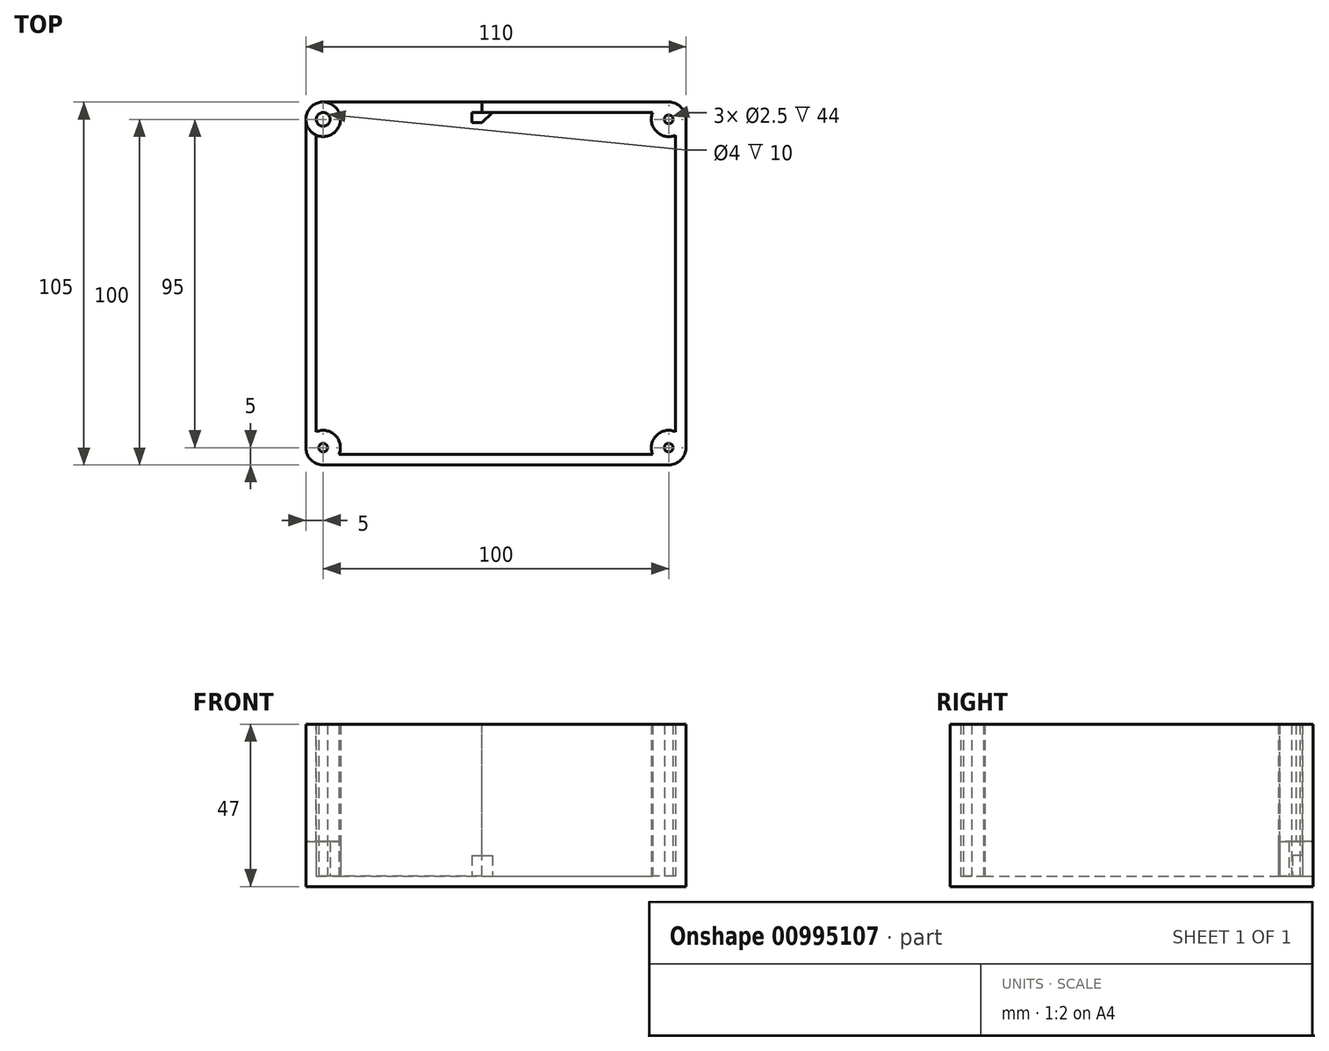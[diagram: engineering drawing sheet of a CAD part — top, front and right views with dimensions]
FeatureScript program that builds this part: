
annotation { "Feature Type Name" : "Feature", "Feature Type Description" : "" }
export const myFeature = defineFeature(function(context is Context, id is Id, definition is map)
    precondition{}
    {
        {
            var Q0;
            Q0=qCreatedBy(makeId("Top.planeOp"),FACE);
            var sketch = newSketch(context, id + "F0", { "sketchPlane" : qUnion([Q0])});
            skLineSegment(sketch, "E0.bottom", {"start": v(-55, -52.5) * mm, "end": v(55, -52.5) * mm});
            skLineSegment(sketch, "E0.top", {"start": v(-55, 52.5) * mm, "end": v(55, 52.5) * mm});
            skLineSegment(sketch, "E0.left", {"start": v(-55, -52.5) * mm, "end": v(-55, 52.5) * mm});
            skLineSegment(sketch, "E0.right", {"start": v(55, -52.5) * mm, "end": v(55, 52.5) * mm});
            skPoint(sketch, "E0.middle", {"position": v(0, 0) * mm});
            skSolve(sketch);
        }
        {
            var Q0;
            Q0 = qSketchRegion(id + "F0", true);
            extrude(context, id + "F1", {"entities" : qUnion([Q0]), "endBound" : BoundingType.SYMMETRIC, "depth" : 47 * mm, "offsetDistance" : 25 * mm});
        }
        {
            var Q0;
            Q0=makeQuery(id+"F1.opExtrude","SWEPT_EDGE",EDGE,{"disambiguationData":[OSD([sQuery(id+"F0.wireOp",EDGE,"E0.bottom"),sQuery(id+"F0.wireOp",EDGE,"E0.right")])]});
            var Q1;
            Q1=makeQuery(id+"F1.opExtrude","SWEPT_EDGE",EDGE,{"disambiguationData":[OSD([sQuery(id+"F0.wireOp",EDGE,"E0.bottom"),sQuery(id+"F0.wireOp",EDGE,"E0.left")])]});
            var Q2;
            Q2=makeQuery(id+"F1.opExtrude","SWEPT_EDGE",EDGE,{"disambiguationData":[OSD([sQuery(id+"F0.wireOp",EDGE,"E0.top"),sQuery(id+"F0.wireOp",EDGE,"E0.left")])]});
            var Q3;
            Q3=makeQuery(id+"F1.opExtrude","SWEPT_EDGE",EDGE,{"disambiguationData":[OSD([sQuery(id+"F0.wireOp",EDGE,"E0.top"),sQuery(id+"F0.wireOp",EDGE,"E0.right")])]});
            fillet(context, id + "F2", {"entities" : qUnion([Q0, Q1, Q2, Q3]), "radius" : 5 * mm, "tangentPropagation" : true, "allowEdgeOverflow" : false});
        }
        {
            var Q0;
            Q0=makeQuery(id+"F1.opExtrude","CAP_FACE",FACE,{"disambiguationData":[OSD([sQuery(id+"F0.wireOp",EDGE,"E0.bottom"),sQuery(id+"F0.wireOp",EDGE,"E0.top"),sQuery(id+"F0.wireOp",EDGE,"E0.left"),sQuery(id+"F0.wireOp",EDGE,"E0.right")])],"isStart":false});
            shell(context, id + "F3", {"entities" : qUnion([Q0]), "thickness" : 3 * mm});
        }
        {
            var Q0;
            Q0=makeQuery(id+"F3.opShell","OFFSET_FACE",FACE,{"disambiguationData":[OSD([sQuery(id+"F0.wireOp",EDGE,"E0.bottom"),sQuery(id+"F0.wireOp",EDGE,"E0.top"),sQuery(id+"F0.wireOp",EDGE,"E0.left"),sQuery(id+"F0.wireOp",EDGE,"E0.right")])]});
            var sketch = newSketch(context, id + "F4", { "sketchPlane" : qUnion([Q0])});
            skCircle(sketch, "E1", {"center": v(-50, -47.5) * mm, "radius": 5 * mm});
            skCircle(sketch, "E2", {"center": v(50, -47.5) * mm, "radius": 5 * mm});
            skCircle(sketch, "E3", {"center": v(50, 47.5) * mm, "radius": 5 * mm});
            skSolve(sketch);
        }
        {
            var Q0;
            Q0 = qSketchRegion(id + "F4", true);
            var Q1;
            Q1=makeQuery(id+"F1.opExtrude","CAP_FACE",FACE,{"disambiguationData":[OSD([sQuery(id+"F0.wireOp",EDGE,"E0.bottom"),sQuery(id+"F0.wireOp",EDGE,"E0.top"),sQuery(id+"F0.wireOp",EDGE,"E0.left"),sQuery(id+"F0.wireOp",EDGE,"E0.right")])],"isStart":false});
            extrude(context, id + "F5", {"entities" : qUnion([Q0]), "operationType" : NewBodyOperationType.ADD, "endBound" : BoundingType.UP_TO_SURFACE, "depth" : 25 * mm, "endBoundEntityFace" : qUnion([Q1]), "offsetDistance" : 25 * mm});
        }
        {
            var Q0;
            Q0=makeQuery(id+"F3.opShell","OFFSET_FACE",FACE,{"disambiguationData":[OSD([sQuery(id+"F0.wireOp",EDGE,"E0.bottom"),sQuery(id+"F0.wireOp",EDGE,"E0.top"),sQuery(id+"F0.wireOp",EDGE,"E0.left"),sQuery(id+"F0.wireOp",EDGE,"E0.right")])]});
            var sketch = newSketch(context, id + "F6", { "sketchPlane" : qUnion([Q0])});
            skCircle(sketch, "E4", {"center": v(-50, -47.5) * mm, "radius": 1.25 * mm});
            skCircle(sketch, "E5", {"center": v(50, -47.5) * mm, "radius": 1.25 * mm});
            skCircle(sketch, "E6", {"center": v(50, 47.5) * mm, "radius": 1.25 * mm});
            skSolve(sketch);
        }
        {
            var Q0;
            Q0 = qSketchRegion(id + "F6", true);
            var Q1;
            Q1=makeQuery(id+"F5.boolean.opBoolean","MERGE",FACE,{"derivedFrom":[makeQuery(id+"F1.opExtrude","CAP_FACE",FACE,{"disambiguationData":[OSD([sQuery(id+"F0.wireOp",EDGE,"E0.bottom"),sQuery(id+"F0.wireOp",EDGE,"E0.top"),sQuery(id+"F0.wireOp",EDGE,"E0.left"),sQuery(id+"F0.wireOp",EDGE,"E0.right")])],"isStart":false}),makeQuery(id+"F5.opExtrude","CAP_FACE",FACE,{"disambiguationData":[OSD([sQuery(id+"F4.wireOp",EDGE,"E1")])],"isStart":false}),makeQuery(id+"F5.opExtrude","CAP_FACE",FACE,{"disambiguationData":[OSD([sQuery(id+"F4.wireOp",EDGE,"E2")])],"isStart":false}),makeQuery(id+"F5.opExtrude","CAP_FACE",FACE,{"disambiguationData":[OSD([sQuery(id+"F4.wireOp",EDGE,"E3")])],"isStart":false}),makeQuery(id+"F5.opExtrude","CAP_FACE",FACE,{"disambiguationData":[OSD([sQuery(id+"F4.wireOp",EDGE,"hSmFbgNi-J2mV-61Hc-GoRM-wuo9VpQavHXK")])],"isStart":false})]});
            extrude(context, id + "F7", {"entities" : qUnion([Q0]), "operationType" : NewBodyOperationType.REMOVE, "endBound" : BoundingType.UP_TO_SURFACE, "depth" : 25 * mm, "endBoundEntityFace" : qUnion([Q1]), "offsetDistance" : 25 * mm});
        }
        {
            var Q0;
            Q0=makeQuery(id+"FNmOlcrzUNOjlDW_1.boolean.opBoolean","MERGE",FACE,{"derivedFrom":[makeQuery(id+"F1.opExtrude","CAP_FACE",FACE,{"disambiguationData":[OSD([sQuery(id+"F0.wireOp",EDGE,"E0.bottom"),sQuery(id+"F0.wireOp",EDGE,"E0.top"),sQuery(id+"F0.wireOp",EDGE,"E0.left"),sQuery(id+"F0.wireOp",EDGE,"E0.right")])],"isStart":false}),makeQuery(id+"FNmOlcrzUNOjlDW_1.opExtrude","CAP_FACE",FACE,{"disambiguationData":[OSD([sQuery(id+"Fl73VWrxdAUel7K_1.wireOp",EDGE,"jCLqAK4i-84Nv-s7N0-ioBH-w4pOyGSMhPc0.bottom"),sQuery(id+"Fl73VWrxdAUel7K_1.wireOp",EDGE,"jCLqAK4i-84Nv-s7N0-ioBH-w4pOyGSMhPc0.top"),sQuery(id+"Fl73VWrxdAUel7K_1.wireOp",EDGE,"jCLqAK4i-84Nv-s7N0-ioBH-w4pOyGSMhPc0.left"),sQuery(id+"Fl73VWrxdAUel7K_1.wireOp",EDGE,"jCLqAK4i-84Nv-s7N0-ioBH-w4pOyGSMhPc0.right"),sQuery(id+"Fl73VWrxdAUel7K_1.wireOp",EDGE,"joEXNwAF-BjP9-4Sa6-PMDD-CcShLHSFX7Nu"),sQuery(id+"Fl73VWrxdAUel7K_1.wireOp",EDGE,"PspjCuC4-ct6j-beC7-JPcA-AMhMl90AcsFd"),sQuery(id+"Fl73VWrxdAUel7K_1.wireOp",EDGE,"BXyMQO9f-R41G-yzOT-ZLec-crP29x3uA3BI"),sQuery(id+"Fl73VWrxdAUel7K_1.wireOp",EDGE,"BY3yu8Kp-6BFw-ywOW-VnpQ-I8gklTRwLebo")])],"isStart":true})]});
            var sketch = newSketch(context, id + "F8", { "sketchPlane" : qUnion([Q0])});
            skLineSegment(sketch, "E7.bottom", {"start": v(-52, 52.5) * mm, "end": v(-4, 52.5) * mm});
            skLineSegment(sketch, "E7.top", {"start": v(-52, 47.5) * mm, "end": v(-4, 47.5) * mm});
            skLineSegment(sketch, "E7.left", {"start": v(-52, 52.5) * mm, "end": v(-52, 47.5) * mm});
            skLineSegment(sketch, "E7.right", {"start": v(-4, 52.5) * mm, "end": v(-4, 47.5) * mm});
            skSolve(sketch);
        }
        {
            var Q0;
            Q0 = qSketchRegion(id + "F8", true);
            var Q1;
            Q1=makeQuery(id+"F3.opShell","OFFSET_FACE",FACE,{"disambiguationData":[OSD([sQuery(id+"F0.wireOp",EDGE,"E0.bottom"),sQuery(id+"F0.wireOp",EDGE,"E0.top"),sQuery(id+"F0.wireOp",EDGE,"E0.left"),sQuery(id+"F0.wireOp",EDGE,"E0.right")])]});
            extrude(context, id + "F9", {"entities" : qUnion([Q0]), "operationType" : NewBodyOperationType.REMOVE, "endBound" : BoundingType.UP_TO_SURFACE, "oppositeDirection" : true, "depth" : 25 * mm, "endBoundEntityFace" : qUnion([Q1]), "offsetDistance" : 25 * mm});
        }
        {
            var Q0;
            Q0=makeQuery(id+"F9.boolean.opBoolean","MERGE",FACE,{"derivedFrom":[makeQuery(id+"F3.opShell","OFFSET_FACE",FACE,{"disambiguationData":[OSD([sQuery(id+"F0.wireOp",EDGE,"E0.bottom"),sQuery(id+"F0.wireOp",EDGE,"E0.top"),sQuery(id+"F0.wireOp",EDGE,"E0.left"),sQuery(id+"F0.wireOp",EDGE,"E0.right")])]})],"fromTools":[makeQuery(id+"F9.opExtrude","CAP_FACE",FACE,{"disambiguationData":[OSD([sQuery(id+"F8.wireOp",EDGE,"E7.bottom"),sQuery(id+"F8.wireOp",EDGE,"E7.top"),sQuery(id+"F8.wireOp",EDGE,"E7.left"),sQuery(id+"F8.wireOp",EDGE,"E7.right")])],"isStart":false})]});
            var sketch = newSketch(context, id + "F10", { "sketchPlane" : qUnion([Q0])});
            skCircle(sketch, "E8", {"center": v(-50, 47.5) * mm, "radius": 5 * mm});
            skCircle(sketch, "E9", {"center": v(-50, 47.5) * mm, "radius": 2 * mm});
            skSolve(sketch);
        }
        {
            var Q0;
            Q0 = qSketchRegion(id + "F10", true);
            extrude(context, id + "F11", {"entities" : qUnion([Q0]), "operationType" : NewBodyOperationType.ADD, "depth" : 10 * mm, "offsetDistance" : 25 * mm});
        }
        {
            var Q0;
            Q0=makeQuery(id+"F5.boolean.opBoolean","MERGE",FACE,{"derivedFrom":[makeQuery(id+"F1.opExtrude","CAP_FACE",FACE,{"disambiguationData":[OSD([sQuery(id+"F0.wireOp",EDGE,"E0.bottom"),sQuery(id+"F0.wireOp",EDGE,"E0.top"),sQuery(id+"F0.wireOp",EDGE,"E0.left"),sQuery(id+"F0.wireOp",EDGE,"E0.right")])],"isStart":false}),makeQuery(id+"F5.opExtrude","CAP_FACE",FACE,{"disambiguationData":[OSD([sQuery(id+"F4.wireOp",EDGE,"E1")])],"isStart":false}),makeQuery(id+"F5.opExtrude","CAP_FACE",FACE,{"disambiguationData":[OSD([sQuery(id+"F4.wireOp",EDGE,"E2")])],"isStart":false}),makeQuery(id+"F5.opExtrude","CAP_FACE",FACE,{"disambiguationData":[OSD([sQuery(id+"F4.wireOp",EDGE,"E3")])],"isStart":false})]});
            var sketch = newSketch(context, id + "F12", { "sketchPlane" : qUnion([Q0])});
            skCircle(sketch, "E10", {"center": v(-50, 47.5) * mm, "radius": 5 * mm});
            skSolve(sketch);
        }
        {
            var Q0;
            Q0 = qSketchRegion(id + "F12", true);
            var Q1;
            Q1=makeQuery(id+"F11.opExtrude","CAP_FACE",FACE,{"disambiguationData":[OSD([sQuery(id+"F10.wireOp",EDGE,"E8"),sQuery(id+"F10.wireOp",EDGE,"E9")])],"isStart":false});
            extrude(context, id + "F13", {"entities" : qUnion([Q0]), "operationType" : NewBodyOperationType.REMOVE, "endBound" : BoundingType.UP_TO_SURFACE, "oppositeDirection" : true, "depth" : 25 * mm, "endBoundEntityFace" : qUnion([Q1]), "offsetDistance" : 25 * mm});
        }
        {
            var Q0;
            {var subQ0=sQuery(id+"F8.wireOp",EDGE,"E7.right");var subQ1=sQuery(id+"F0.wireOp",EDGE,"E0.bottom");var subQ2=sQuery(id+"F0.wireOp",EDGE,"E0.right");var subQ3=sQuery(id+"F0.wireOp",EDGE,"E0.top");var subQ4=sQuery(id+"F0.wireOp",EDGE,"E0.left");Q0=makeQuery(id+"F11.boolean.opBoolean","SPLIT",FACE,{"disambiguationData":[TD([makeQuery(id+"F1.opExtrude","SWEPT_FACE",FACE,{"disambiguationData":[OSD([subQ3])]})])],"derivedFrom":makeQuery(id+"F9.boolean.opBoolean","MERGE",FACE,{"derivedFrom":[makeQuery(id+"F3.opShell","OFFSET_FACE",FACE,{"disambiguationData":[OSD([subQ1,subQ3,subQ4,subQ2])]})],"fromTools":[makeQuery(id+"F9.opExtrude","CAP_FACE",FACE,{"disambiguationData":[OSD([sQuery(id+"F8.wireOp",EDGE,"E7.bottom"),sQuery(id+"F8.wireOp",EDGE,"E7.top"),sQuery(id+"F8.wireOp",EDGE,"E7.left"),subQ0])],"isStart":false})]})});}
            var sketch = newSketch(context, id + "F14", { "sketchPlane" : qUnion([Q0])});
            skLineSegment(sketch, "E11.bottom", {"start": v(-1, 49.5) * mm, "end": v(-7, 49.5) * mm});
            skLineSegment(sketch, "E11.top", {"start": v(-1, 46.5) * mm, "end": v(-7, 46.5) * mm});
            skLineSegment(sketch, "E11.left", {"start": v(-1, 49.5) * mm, "end": v(-1, 46.5) * mm});
            skLineSegment(sketch, "E11.right", {"start": v(-7, 49.5) * mm, "end": v(-7, 46.5) * mm});
            skSolve(sketch);
        }
        {
            var Q0;
            Q0 = qSketchRegion(id + "F14", true);
            extrude(context, id + "F15", {"entities" : qUnion([Q0]), "operationType" : NewBodyOperationType.ADD, "depth" : 6 * mm, "offsetDistance" : 25 * mm});
        }
        {
            var Q0;
            Q0=makeQuery(id+"F15.opExtrude","SWEPT_EDGE",EDGE,{"disambiguationData":[OSD([sQuery(id+"F14.wireOp",EDGE,"E11.top"),sQuery(id+"F14.wireOp",EDGE,"E11.left")])]});
            chamfer(context, id + "F16", {"entities" : qUnion([Q0]), "width" : 3 * mm, "tangentPropagation" : true});
        }
    });
